# Revit family: P30 DT Pendant Loudspeaker
name_source: partatom
category: Communication Devices
revit_build: Autodesk Revit 2017 (Build: 20190507_1515(x64)
units: mm (PartAtom-declared; Revit-internal decimal feet)

## family parameters
Always vertical = Yes
Cut with Voids When Loaded = No
Maintain Annotation Orientation = No
Part Type = Normal
Room Calculation Point = No
Round Connector Dimension = Use Diameter
Shared = No
Work Plane-Based = No

## types (1)
- P30DT
    Accessories (included) = Two wire suspension cables; Two Gripple cable fastners: End cap and cable cover
    Compliance = ETL listed to comply with UL std 1480A, 
Certified to CSA C22.2#62368-1

Suspension system and Gripple cable fasteners listed per
UL1598 and UL2239, TUV and CSA Class 3426-01 and Class
3426-81.
    Continuous Power Handling @ Nominal Impedance = Passive / 28V / 50W @16 ohms (200W peak)
    Controls = Power tap / low impedance selector switch
    Description = Default
    Dimensions H x W (diameter) = 223 mm x 233mm (8.78" x 9.17")
    Finish = ABS plastic, matte finish, White or Black
    Grille = Powder-coated perforated steel
White (RAL 9011) or Black (RAL 9010) finish
    Input Connection = 4-way Euroblock connector with permanent pass-through
    Manufacturer = Biamp
    Model = P30DT
    Mounting Provisions = Two 5m (16.4 ft) wire suspension cables (one as primary support, one as a safety cable), of high tensile galavized steel wire rope with integrated spring clips for attaching the cable to the bracket and Gripple cable fasteners.
    Nominal Beamwidth (H x V) = 120°, conical
    Nominal Maximum SPL @ 1m = Passive / Peak - 110 db / Continuous - 104 dB
    Nominal Sensitivity @ 1m = Passive / @1W - 87 dB / @2.83V - 84 dB
    Operating Environment = Indoor
    Operating Mode = Passive
    Operating Range (-10dB) = 75 Hz to 20 kHz
    Protection = Self-resetting loudspeaker protection
    Recommended Accessories = 75 Hz, 12db/Oct High Pass
    Recommended Amplifiers = 50W - 100W @ 16 ohms, (28V - 40V)
    Transducers = LF1 x 42.5" (108mm) coated paper cone / HF1 x 1" (25mm) soft dome
    Transformer - 100V = 30W, 15W, 7.5W, 3.75W
    Transformer - 70V = 30W, 15W, 7.5W, 3.75W, 1.75W
    Type Comments = Not Used
    URL = Default
    Unit Weight = 2.6 kg (5.7 lbs)

## geometry (parser evidence)
native form markers: Blend x4, Sweep x2
no freeform markers — native parametric forms only
